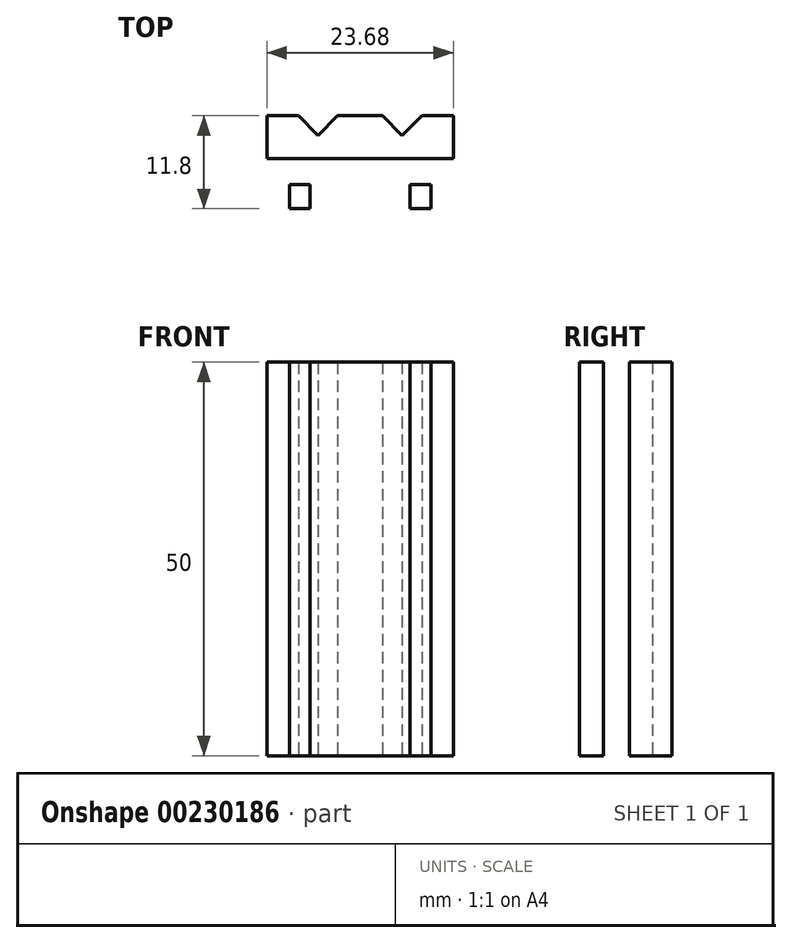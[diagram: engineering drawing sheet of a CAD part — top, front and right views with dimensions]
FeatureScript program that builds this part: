
annotation { "Feature Type Name" : "Feature", "Feature Type Description" : "" }
export const myFeature = defineFeature(function(context is Context, id is Id, definition is map)
    precondition{}
    {
        {
            var Q0;
            Q0=qCreatedBy(makeId("Top.planeOp"),FACE);
            var sketch = newSketch(context, id + "F0", { "sketchPlane" : qUnion([Q0])});
            skLineSegment(sketch, "E0.bottom", {"start": v(-11.84, 5.9) * mm, "end": v(11.84, 5.9) * mm});
            skLineSegment(sketch, "E0.top", {"start": v(-11.84, -5.9) * mm, "end": v(11.84, -5.9) * mm});
            skLineSegment(sketch, "E0.left", {"start": v(-11.84, 5.9) * mm, "end": v(-11.84, -5.9) * mm});
            skLineSegment(sketch, "E0.right", {"start": v(11.84, 5.9) * mm, "end": v(11.84, -5.9) * mm});
            skPoint(sketch, "E0.middle", {"position": v(0, 0) * mm});
            skLineSegment(sketch, "E1.top", {"start": v(-11.84, 0.49) * mm, "end": v(11.84, 0.49) * mm});
            skLineSegment(sketch, "E1.left", {"start": v(-11.84, 5.9) * mm, "end": v(-11.84, 0.49) * mm});
            skLineSegment(sketch, "E1.right", {"start": v(11.84, 5.9) * mm, "end": v(11.84, 0.49) * mm});
            skLineSegment(sketch, "E2.bottom", {"start": v(-9, 0.49) * mm, "end": v(-11.84, 0.49) * mm});
            skLineSegment(sketch, "E2.top", {"start": v(-9, -5.9) * mm, "end": v(-11.84, -5.9) * mm});
            skLineSegment(sketch, "E2.left", {"start": v(-9, 0.49) * mm, "end": v(-9, -5.9) * mm});
            skLineSegment(sketch, "E2.right", {"start": v(-11.84, 0.49) * mm, "end": v(-11.84, -5.9) * mm});
            skLineSegment(sketch, "E3.bottom", {"start": v(9, 0.49) * mm, "end": v(11.84, 0.49) * mm});
            skLineSegment(sketch, "E3.top", {"start": v(9, -5.9) * mm, "end": v(11.84, -5.9) * mm});
            skLineSegment(sketch, "E3.left", {"start": v(9, 0.49) * mm, "end": v(9, -5.9) * mm});
            skLineSegment(sketch, "E3.right", {"start": v(11.84, 0.49) * mm, "end": v(11.84, -5.9) * mm});
            skLineSegment(sketch, "E4.bottom", {"start": v(9, -2.83) * mm, "end": v(6.34, -2.83) * mm});
            skLineSegment(sketch, "E4.top", {"start": v(9, -5.9) * mm, "end": v(6.34, -5.9) * mm});
            skLineSegment(sketch, "E4.left", {"start": v(8.99, -2.83) * mm, "end": v(8.99, -5.9) * mm});
            skLineSegment(sketch, "E4.right", {"start": v(6.34, -2.83) * mm, "end": v(6.34, -5.9) * mm});
            skLineSegment(sketch, "E5.bottom", {"start": v(-9, -2.83) * mm, "end": v(-6.34, -2.83) * mm});
            skLineSegment(sketch, "E5.top", {"start": v(-9, -5.9) * mm, "end": v(-6.34, -5.9) * mm});
            skLineSegment(sketch, "E5.left", {"start": v(-9, -2.83) * mm, "end": v(-9, -5.9) * mm});
            skLineSegment(sketch, "E5.right", {"start": v(-6.34, -2.83) * mm, "end": v(-6.34, -5.9) * mm});
            skLineSegment(sketch, "E6", {"start": v(-7.84, 5.9) * mm, "end": v(-5.34, 3.4) * mm});
            skLineSegment(sketch, "E7", {"start": v(-5.34, 3.4) * mm, "end": v(-2.84, 5.9) * mm});
            skLineSegment(sketch, "E8", {"start": v(7.84, 5.9) * mm, "end": v(5.34, 3.4) * mm});
            skLineSegment(sketch, "E9", {"start": v(5.34, 3.4) * mm, "end": v(2.84, 5.9) * mm});
            skLineSegment(sketch, "E10", {"start": v(-11.84, 5.9) * mm, "end": v(-7.84, 5.9) * mm});
            skLineSegment(sketch, "E11", {"start": v(7.84, 5.9) * mm, "end": v(11.84, 5.9) * mm});
            skSolve(sketch);
        }
        {
            var Q0;
            Q0=makeQuery(id+"F0.imprint","IMPRINT",FACE,{"disambiguationData":[TD([[makeQuery(id+"F0.imprint","IMPRINT",EDGE,{"derivedFrom":sQuery(id+"F0.wireOp",EDGE,"E2.bottom")}),1.0]])]});
            var Q1;
            Q1=makeQuery(id+"F0.imprint","IMPRINT",FACE,{"disambiguationData":[TD([[makeQuery(id+"F0.imprint","IMPRINT",EDGE,{"derivedFrom":sQuery(id+"F0.wireOp",EDGE,"E1.top")}),1.0]])]});
            var Q2;
            Q2=makeQuery(id+"F0.imprint","IMPRINT",FACE,{"disambiguationData":[TD([[makeQuery(id+"F0.imprint","IMPRINT",EDGE,{"derivedFrom":sQuery(id+"F0.wireOp",EDGE,"E3.bottom")}),-1.0]])]});
            var Q3;
            Q3=makeQuery(id+"F0.imprint","IMPRINT",FACE,{"disambiguationData":[TD([[makeQuery(id+"F0.imprint","IMPRINT",EDGE,{"derivedFrom":sQuery(id+"F0.wireOp",EDGE,"E4.bottom")}),1.0]])]});
            var Q4;
            Q4=makeQuery(id+"F0.imprint","IMPRINT",FACE,{"disambiguationData":[TD([[makeQuery(id+"F0.imprint","IMPRINT",EDGE,{"derivedFrom":sQuery(id+"F0.wireOp",EDGE,"E5.bottom")}),-1.0]])]});
            extrude(context, id + "F1", {"entities" : qUnion([Q0, Q1, Q2, Q3, Q4]), "depth" : 50 * mm});
        }
    });
